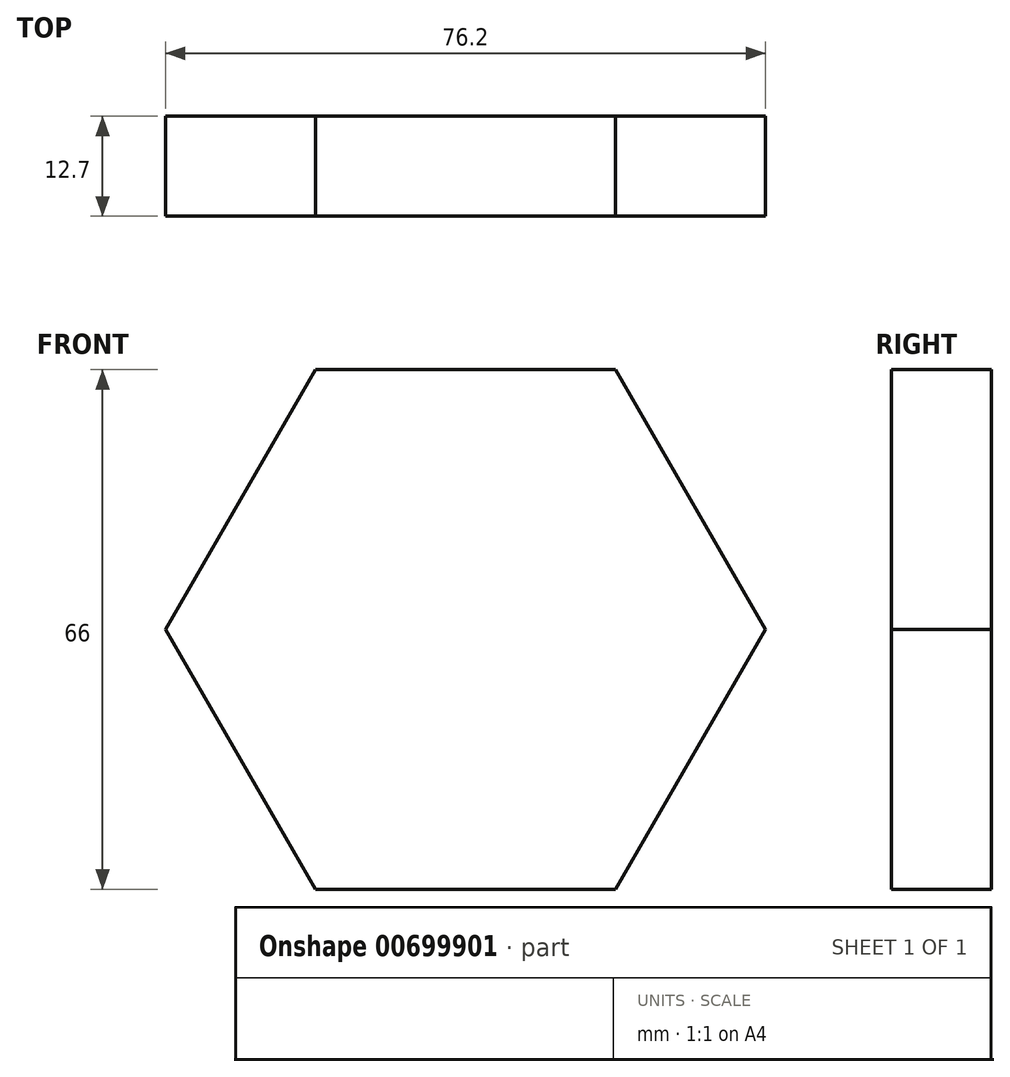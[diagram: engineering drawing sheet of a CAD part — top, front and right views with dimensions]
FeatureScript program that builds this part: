
annotation { "Feature Type Name" : "Feature", "Feature Type Description" : "" }
export const myFeature = defineFeature(function(context is Context, id is Id, definition is map)
    precondition{}
    {
        {
            var Q0;
            Q0=qCreatedBy(makeId("Front.planeOp"),FACE);
            var sketch = newSketch(context, id + "F0", { "sketchPlane" : qUnion([Q0])});
            skCircle(sketch, "E0.cCircle", {"center": v(0, 0) * mm, "radius": 33 * mm, "construction": true});
            skLineSegment(sketch, "E0.0", {"start": v(19.05, 33) * mm, "end": v(38.1, 0) * mm});
            skLineSegment(sketch, "E0.1", {"start": v(38.1, 0) * mm, "end": v(19.05, -33) * mm});
            skLineSegment(sketch, "E0.2", {"start": v(19.05, -33) * mm, "end": v(-19.05, -33) * mm});
            skLineSegment(sketch, "E0.3", {"start": v(-19.05, -33) * mm, "end": v(-38.1, 0) * mm});
            skLineSegment(sketch, "E0.4", {"start": v(-38.1, 0) * mm, "end": v(-19.05, 33) * mm});
            skLineSegment(sketch, "E0.5", {"start": v(-19.05, 33) * mm, "end": v(19.05, 33) * mm});
            skPoint(sketch, "E0.0.midPoint", {"position": v(28.57, 16.5) * mm});
            skSolve(sketch);
        }
        {
            var Q0;
            Q0=makeQuery(id+"F0.imprint","IMPRINT",FACE,{"disambiguationData":[TD([[makeQuery(id+"F0.imprint","IMPRINT",EDGE,{"derivedFrom":sQuery(id+"F0.wireOp",EDGE,"E0.0")}),-1.0]])]});
            extrude(context, id + "F1", {"entities" : qUnion([Q0]), "depth" : 12.7 * mm, "offsetDistance" : 25.4 * mm});
        }
    });
